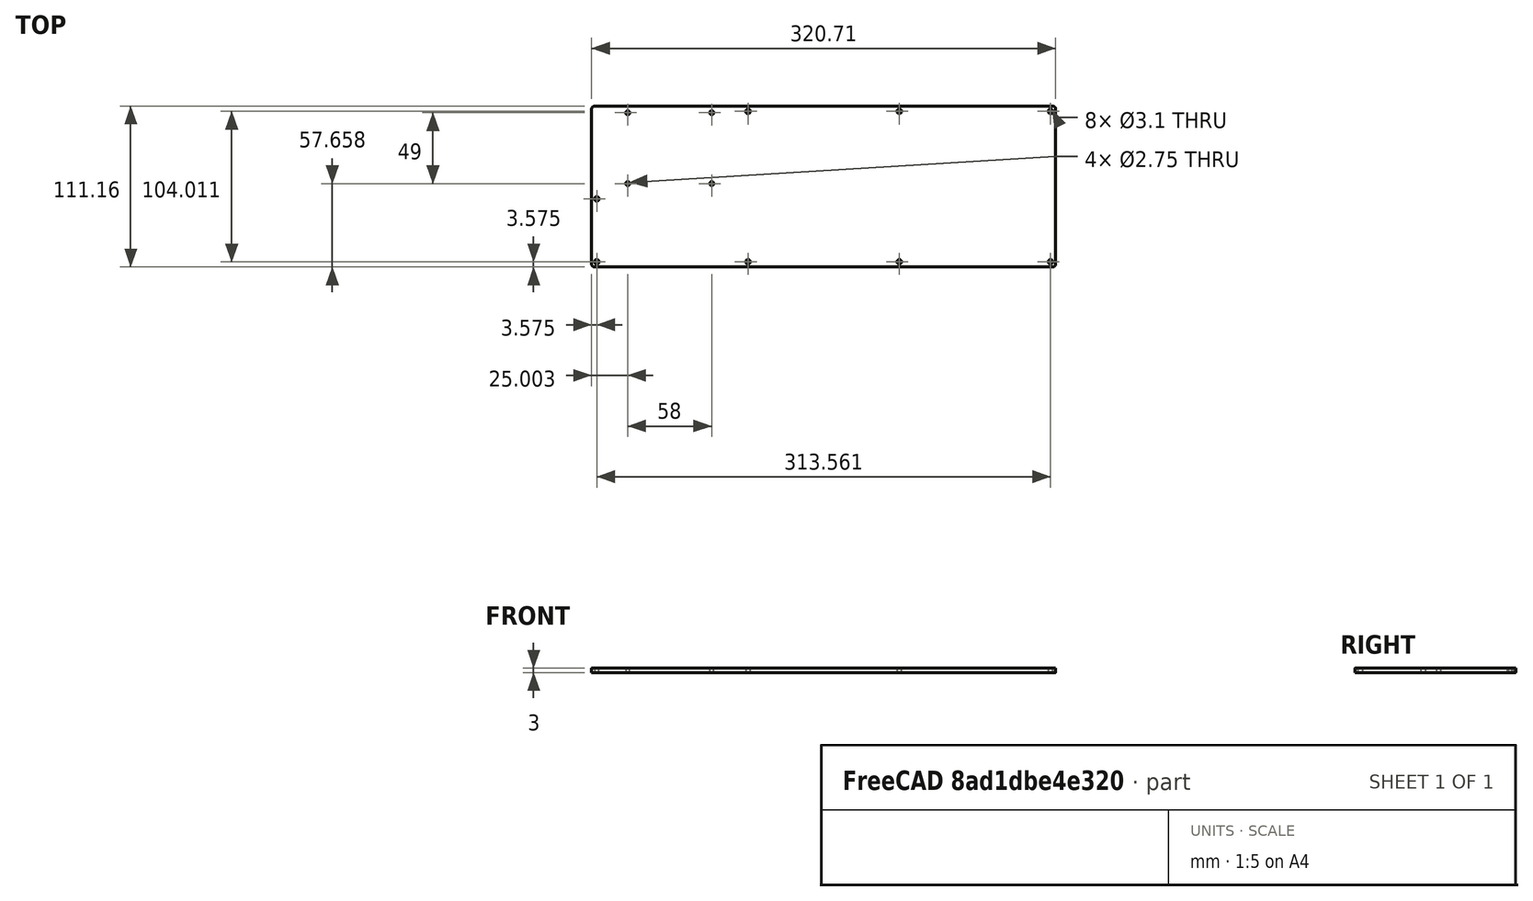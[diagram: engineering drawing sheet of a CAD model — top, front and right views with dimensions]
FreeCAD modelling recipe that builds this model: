
FCSTD DOCUMENT  (FreeCAD 0.19R24366 (Git))
Label: bottom_layer
License: All rights reserved
LicenseURL: http://en.wikipedia.org/wiki/All_rights_reserved
objects: Sketcher::SketchObject×1, PartDesign::Pad×1, PartDesign::Body×1, PartDesign::CoordinateSystem×1, App::Part×1
note: 5 computed .brp shape members not serialized (recipe doc carries the construction recipe); baked Part::Feature solids carry a one-line shape summary decoded from their .brp
EXTERNAL_REF file=../master.FCStd obj=Spreadsheet

FEATURE [Sketcher::SketchObject] Sketch001  label="bottom_layer_sketch"
  FullyConstrained = true
  MapMode = 5
  Support = -> [XY_Plane]
  expr: Constraints[94] = 0
  expr: Constraints[59] = ((<<master>>#<<inputs>>.key_width + <<master>>#<<inputs>>.horizontal_key_spacing) * 15 + <<master>>#<<inputs>>.key_width + <<master>>#<<inputs>>.right_edge_padding - <<master>>#<<inputs>>.wall_thickness / 2 + <<master>>#<<inputs>>.left_edge_padding - <<master>>#<<inputs>>.wall_thickness / 2) / 3
  expr: Constraints[73] = <<master>>#<<inputs>>.wall_thickness / 2
  expr: Constraints[89] = <<master>>#<<inputs>>.hyperpixel_left_hole_padding
  expr: Constraints[84] = <<master>>#<<inputs>>.raspberry_pi_4_mounting_hole_diameter / 2
  expr: Constraints[80] = <<master>>#<<inputs>>.hyperpixel_width
  expr: Constraints[61] = 0
  expr: Constraints[53] = (<<master>>#<<inputs>>.key_height + <<master>>#<<inputs>>.vertical_key_spacing) * 4 + <<master>>#<<inputs>>.bottom_edge_padding - <<master>>#<<inputs>>.wall_thickness / 2 + <<master>>#<<inputs>>.key_height
  expr: Constraints[90] = <<master>>#<<inputs>>.hyperpixel_bottom_hole_padding
  expr: Constraints[79] = <<master>>#<<inputs>>.hyperpixel_height
  expr: Constraints[54] = <<master>>#<<inputs>>.bottom_edge_padding
  expr: Constraints[93] = <<master>>#<<inputs>>.hyperpixel_right_hole_padding
  expr: Constraints[22] = (<<master>>#<<inputs>>.key_width + <<master>>#<<inputs>>.horizontal_key_spacing) * 15
  expr: Constraints[55] = <<master>>#<<inputs>>.left_edge_padding - <<master>>#<<inputs>>.wall_thickness / 2
  expr: Constraints[9] = <<master>>#<<inputs>>.key_height
  expr: Constraints[56] = <<master>>#<<inputs>>.right_edge_padding
  expr: Constraints[8] = <<master>>#<<inputs>>.key_width
  expr: Constraints[60] = 0
  expr: Constraints[35] = (<<master>>#<<inputs>>.key_height + <<master>>#<<inputs>>.vertical_key_spacing) * 4
  expr: Constraints[88] = <<master>>#<<inputs>>.hyperpixel_top_hole_padding
  expr: Constraints[62] = ((<<master>>#<<inputs>>.key_width + <<master>>#<<inputs>>.horizontal_key_spacing) * 15 + <<master>>#<<inputs>>.key_width + <<master>>#<<inputs>>.right_edge_padding - <<master>>#<<inputs>>.wall_thickness / 2 + <<master>>#<<inputs>>.left_edge_padding - <<master>>#<<inputs>>.wall_thickness / 2) / 3
  expr: Constraints[66] = <<master>>#<<inputs>>.top_edge_padding - <<master>>#<<inputs>>.wall_thickness / 2
  expr: Constraints[46] = <<master>>#<<inputs>>.edge_fillet_radius
  expr: Constraints[71] = 0
  expr: Constraints[49] = <<master>>#<<inputs>>.mounting_hole_diameter / 2
  expr: Constraints[58] = <<master>>#<<inputs>>.wall_thickness / 2
  expr: Constraints[72] = <<master>>#<<inputs>>.wall_thickness / 2
  expr: Constraints[98] = (<<master>>#<<inputs>>.key_height + <<master>>#<<inputs>>.vertical_key_spacing) * 3 - <<master>>#<<inputs>>.wall_thickness / 2
  sketch-geometry (35):
    g0: LineSegment StartX=-7 StartY=7 StartZ=0 EndX=7 EndY=7 EndZ=0
    g1: LineSegment StartX=7 StartY=7 StartZ=0 EndX=7 EndY=-7 EndZ=0
    g2: LineSegment StartX=7 StartY=-7 StartZ=0 EndX=-7 EndY=-7 EndZ=0
    g3: LineSegment StartX=-7 StartY=-7 StartZ=0 EndX=-7 EndY=7 EndZ=0
    g4: LineSegment StartX=278.75 StartY=7 StartZ=0 EndX=292.75 EndY=7 EndZ=0
    g5: LineSegment StartX=292.75 StartY=7 StartZ=0 EndX=292.75 EndY=-7 EndZ=0
    g6: LineSegment StartX=292.75 StartY=-7 StartZ=0 EndX=278.75 EndY=-7 EndZ=0
    g7: LineSegment StartX=278.75 StartY=-7 StartZ=0 EndX=278.75 EndY=7 EndZ=0
    g8: GeomPoint X=278.75 Y=7 Z=0
    g9: LineSegment StartX=-7 StartY=-69.2 StartZ=0 EndX=7 EndY=-69.2 EndZ=0
    g10: LineSegment StartX=7 StartY=-69.2 StartZ=0 EndX=7 EndY=-83.2 EndZ=0
    g11: LineSegment StartX=7 StartY=-83.2 StartZ=0 EndX=-7 EndY=-83.2 EndZ=0
    g12: LineSegment StartX=-7 StartY=-83.2 StartZ=0 EndX=-7 EndY=-69.2 EndZ=0
    g13: LineSegment StartX=-15.4775 StartY=17.4775 StartZ=0 EndX=301.228 EndY=17.4775 EndZ=0
    g14: LineSegment StartX=303.228 StartY=15.4775 StartZ=0 EndX=303.228 EndY=-91.6775 EndZ=0
    g15: LineSegment StartX=301.228 StartY=-93.6775 StartZ=0 EndX=-15.4775 EndY=-93.6775 EndZ=0
    g16: LineSegment StartX=-17.4775 StartY=-91.6775 StartZ=0 EndX=-17.4775 EndY=15.4775 EndZ=0
    g17: ArcOfCircle CenterX=301.228 CenterY=15.4775 CenterZ=0 NormalX=0 NormalY=0 NormalZ=1 AngleXU=0 Radius=2 StartAngle=0 EndAngle=1.5708
    g18: ArcOfCircle CenterX=301.228 CenterY=-91.6775 CenterZ=0 NormalX=0 NormalY=0 NormalZ=1 AngleXU=0 Radius=2 StartAngle=4.71239 EndAngle=6.28319
    g19: ArcOfCircle CenterX=-15.4775 CenterY=-91.6775 CenterZ=0 NormalX=0 NormalY=0 NormalZ=1 AngleXU=0 Radius=2 StartAngle=3.14159 EndAngle=4.71239
    g20: Circle CenterX=-13.9055 CenterY=-90.1055 CenterZ=0 NormalX=0 NormalY=0 NormalZ=1 AngleXU=0 Radius=1.55
    g21: Circle CenterX=195.135 CenterY=-90.1055 CenterZ=0 NormalX=0 NormalY=0 NormalZ=1 AngleXU=0 Radius=1.55
    g22: Circle CenterX=299.656 CenterY=-90.1055 CenterZ=0 NormalX=0 NormalY=0 NormalZ=1 AngleXU=0 Radius=1.55
    g23: Circle CenterX=90.6148 CenterY=-90.1055 CenterZ=0 NormalX=0 NormalY=0 NormalZ=1 AngleXU=0 Radius=1.55
    g24: Circle CenterX=90.6148 CenterY=13.9055 CenterZ=0 NormalX=0 NormalY=0 NormalZ=1 AngleXU=0 Radius=1.55
    g25: Circle CenterX=195.135 CenterY=13.9055 CenterZ=0 NormalX=0 NormalY=0 NormalZ=1 AngleXU=0 Radius=1.55
    g26: Circle CenterX=299.656 CenterY=13.9055 CenterZ=0 NormalX=0 NormalY=0 NormalZ=1 AngleXU=0 Radius=1.55
    g27: ArcOfCircle CenterX=-15.4775 CenterY=15.4775 CenterZ=0 NormalX=0 NormalY=0 NormalZ=1 AngleXU=0 Radius=2 StartAngle=1.5708 EndAngle=3.14159
    g28: LineSegment StartX=-17.4775 StartY=-40.7225 StartZ=0 EndX=80.5225 EndY=-40.7225 EndZ=0
    g29: LineSegment StartX=80.5225 StartY=17.4775 StartZ=0 EndX=80.5225 EndY=-40.7225 EndZ=0
    g30: Circle CenterX=7.5225 CenterY=12.9775 CenterZ=0 NormalX=0 NormalY=0 NormalZ=1 AngleXU=0 Radius=1.375
    g31: Circle CenterX=65.5225 CenterY=12.9775 CenterZ=0 NormalX=0 NormalY=0 NormalZ=1 AngleXU=0 Radius=1.375
    g32: Circle CenterX=7.5225 CenterY=-36.0225 CenterZ=0 NormalX=0 NormalY=0 NormalZ=1 AngleXU=0 Radius=1.375
    g33: Circle CenterX=65.5225 CenterY=-36.0225 CenterZ=0 NormalX=0 NormalY=0 NormalZ=1 AngleXU=0 Radius=1.375
    g34: Circle CenterX=-13.9055 CenterY=-46.578 CenterZ=0 NormalX=0 NormalY=0 NormalZ=1 AngleXU=0 Radius=1.55
  constraints (99):
    c: Coincident(g0,g1)
    c: Coincident(g1,g2)
    c: Coincident(g2,g3)
    c: Coincident(g3,g0)
    c: Horizontal(g0)
    c: Horizontal(g2)
    c: Vertical(g1)
    c: Vertical(g3)
    c: Distance(g0) = 14
    c: Distance(g3) = 14
    c: Symmetric(g0,g1,g-1)
    c: Coincident(g4,g5)
    c: Coincident(g5,g6)
    c: Coincident(g6,g7)
    c: Coincident(g7,g4)
    c: Horizontal(g4)
    c: Horizontal(g6)
    c: Vertical(g5)
    c: Vertical(g7)
    c: Equal(g3,g7)
    c: Equal(g0,g4)
    c: DistanceY(g0,g8) = 0
    c: DistanceX(g0,g8) = 285.75
    c: Coincident(g4,g8)
    c: Coincident(g9,g10)
    c: Coincident(g10,g11)
    c: Coincident(g11,g12)
    c: Coincident(g12,g9)
    c: Horizontal(g9)
    c: Horizontal(g11)
    c: Vertical(g10)
    c: Vertical(g12)
    c: Equal(g0,g9)
    c: Equal(g3,g12)
    c: DistanceX(g0,g9) = 0
    c: DistanceY(g9,g0) = 76.2
    c: Horizontal(g13)
    c: Horizontal(g15)
    c: Vertical(g14)
    c: Vertical(g16)
    c: Tangent(g13,g17) = 1.5708
    c: Tangent(g14,g17) = 1.5708
    c: Tangent(g14,g18) = 1.5708
    c: Tangent(g15,g18) = 1.5708
    c: Tangent(g15,g19) = 1.5708
    c: Tangent(g16,g19) = 1.5708
    c: Radius(g19) = 2
    c: Equal(g19,g18)
    c: Equal(g17,g18)
    c: Radius(g20) = 1.55
    c: Equal(g20,g21)
    c: Equal(g21,g22)
    c: Equal(g21,g23)
    c: DistanceY(g20,g0) = 97.1055
    c: DistanceY(g15,g11) = 10.4775
    c: DistanceX(g20,g0) = 6.9055
    c: DistanceX(g4,g14) = 10.4775
    c: DistanceY(g20,g22) = 0
    c: DistanceX(g22,g14) = 3.572
    c: DistanceX(g20,g23) = 104.52
    c: DistanceY(g23,g20) = 0
    c: DistanceY(g23,g21) = 0
    c: DistanceX(g21,g22) = 104.52
    c: Equal(g21,g26)
    c: Equal(g26,g25)
    c: Equal(g26,g24)
    c: DistanceY(g8,g26) = 6.9055
    c: DistanceX(g26,g22) = 0
    c: DistanceX(g25,g21) = 0
    c: DistanceY(g25,g26) = 0
    c: DistanceX(g23,g24) = 0
    c: DistanceY(g24,g25) = 0
    c: DistanceY(g26,g13) = 3.572
    c: DistanceX(g16,g20) = 3.572
    c: Tangent(g13,g27) = 1.5708
    c: Tangent(g16,g27) = 1.5708
    c: Equal(g27,g19)
    c: Horizontal(g28)
    c: PointOnObject(g28,g16)
    c: DistanceY(g28,g13) = 58.2
    c: Distance(g28) = 98
    c: Perpendicular(g28,g29)
    c: Coincident(g29,g28)
    c: PointOnObject(g29,g13)
    c: Radius(g30) = 1.375
    c: Equal(g31,g30)
    c: Equal(g32,g30)
    c: Equal(g30,g33)
    c: DistanceY(g30,g13) = 4.5
    c: DistanceX(g16,g30) = 25
    c: DistanceY(g28,g32) = 4.7
    c: DistanceX(g30,g32) = 0
    c: DistanceY(g31,g30) = 0
    c: DistanceX(g31,g29) = 15
    c: DistanceY(g32,g33) = 0
    c: DistanceX(g33,g31) = 0
    c: Equal(g20,g34)
    c: DistanceX(g20,g34) = 0
    c: DistanceY(g34,g0) = 53.578
FEATURE [PartDesign::Pad] Pad  label="bottom_layer_pad"
  Direction = (1,1,1)
  Length = 3
  Length2 = 100
  Profile = -> Sketch001
  Type = 0
  expr: Length = <<master>>#<<inputs>>.bottom_layer_thickness
FEATURE [PartDesign::Body] Body  label="bottom_layer_body"
  Group = -> [Sketch001,Pad]
  Origin = -> Origin
  Tip = -> Pad
FEATURE [PartDesign::CoordinateSystem] bottom_layer_lcs
  AttacherType = Attacher::AttachEngine3D
  MapMode = 5
  Placement = pos=(0,0,3) rot=(0,0,1;0rad)
  Support = -> [Pad]
FEATURE [App::Part] Part  label="bottom_layer_part"
  Group = -> [Body,bottom_layer_lcs]
  Origin = -> Origin001
